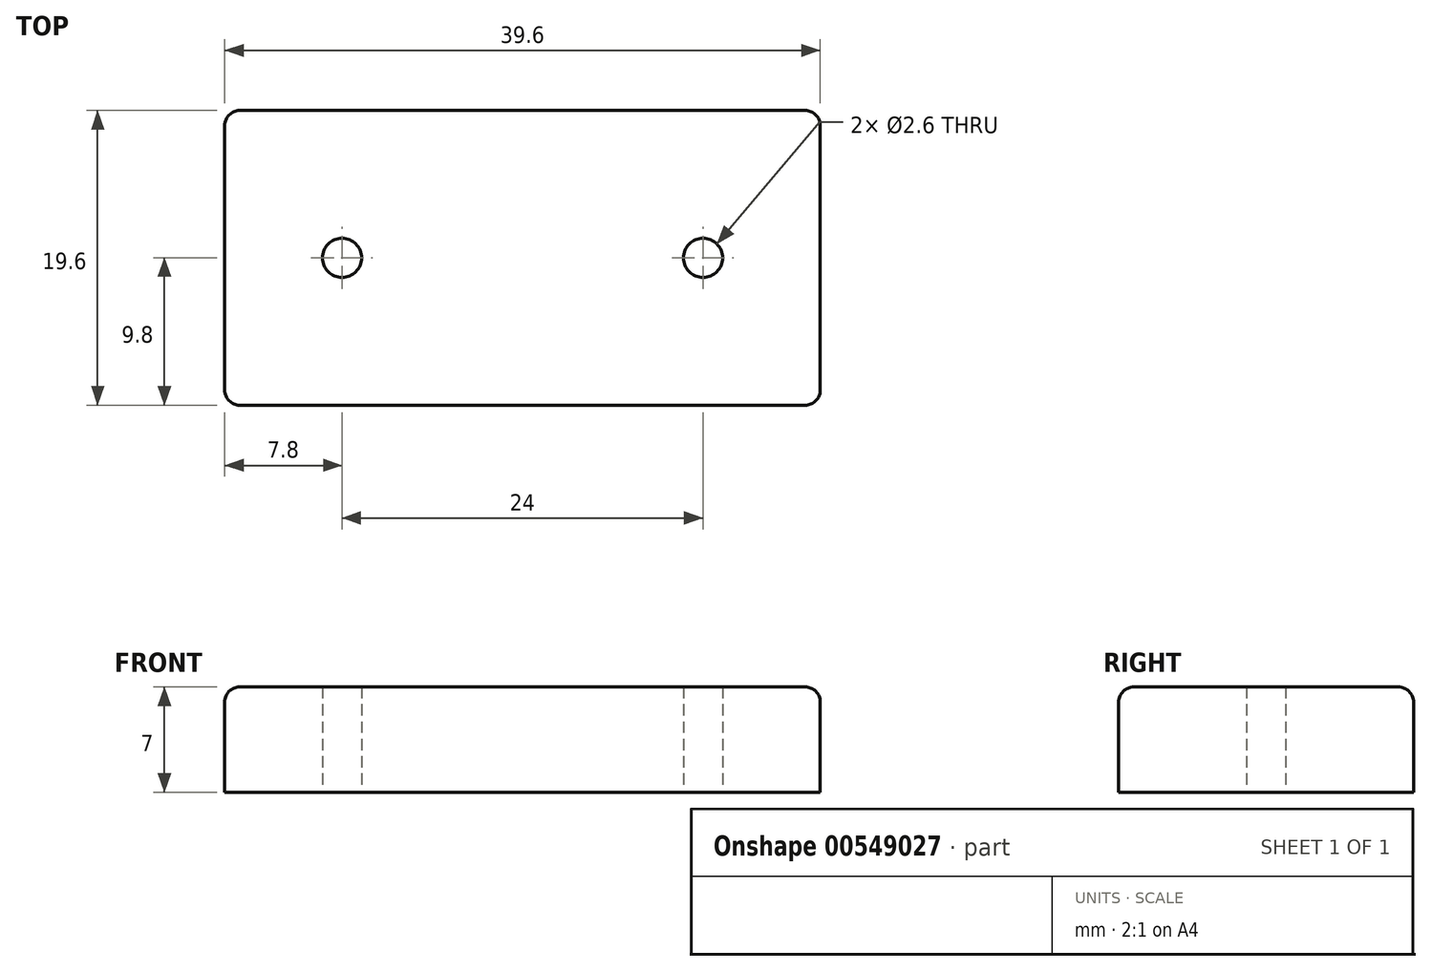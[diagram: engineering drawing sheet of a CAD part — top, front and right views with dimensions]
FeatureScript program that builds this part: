
annotation { "Feature Type Name" : "Feature", "Feature Type Description" : "" }
export const myFeature = defineFeature(function(context is Context, id is Id, definition is map)
    precondition{}
    {
        {
            var Q0;
            Q0=qCreatedBy(makeId("Top.planeOp"),FACE);
            var sketch = newSketch(context, id + "F0", { "sketchPlane" : qUnion([Q0])});
            skLineSegment(sketch, "E0.bottom", {"start": v(19.8, -9.8) * mm, "end": v(-19.8, -9.8) * mm});
            skLineSegment(sketch, "E0.top", {"start": v(19.8, 9.8) * mm, "end": v(-19.8, 9.8) * mm});
            skLineSegment(sketch, "E0.left", {"start": v(19.8, -9.8) * mm, "end": v(19.8, 9.8) * mm});
            skLineSegment(sketch, "E0.right", {"start": v(-19.8, -9.8) * mm, "end": v(-19.8, 9.8) * mm});
            skPoint(sketch, "E0.middle", {"position": v(0, 0) * mm});
            skCircle(sketch, "E1", {"center": v(12, 0) * mm, "radius": 1.3 * mm});
            skLineSegment(sketch, "E2", {"start": v(0, 0) * mm, "end": v(0, 13.8) * mm, "construction": true});
            skPoint(sketch, "E2.endSnap0", {"position": v(0, 9.8) * mm});
            skCircle(sketch, "E3.MirrorC", {"center": v(-12, 0) * mm, "radius": 1.3 * mm});
            skSolve(sketch);
        }
        {
            var Q0;
            Q0=makeQuery(id+"F0.imprint","IMPRINT",FACE,{"disambiguationData":[TD([[makeQuery(id+"F0.imprint","IMPRINT",EDGE,{"derivedFrom":sQuery(id+"F0.wireOp",EDGE,"E0.bottom")}),-1.0]])]});
            extrude(context, id + "F1", {"entities" : qUnion([Q0]), "depth" : 7 * mm, "offsetDistance" : 25 * mm});
        }
        {
            var Q0;
            Q0=makeQuery(id+"F1.opExtrude","CAP_EDGE",EDGE,{"disambiguationData":[OSD([sQuery(id+"F0.wireOp",EDGE,"E0.top")])],"isStart":false});
            var Q1;
            Q1=makeQuery(id+"F1.opExtrude","CAP_EDGE",EDGE,{"disambiguationData":[OSD([sQuery(id+"F0.wireOp",EDGE,"E0.left")])],"isStart":false});
            var Q2;
            Q2=makeQuery(id+"F1.opExtrude","CAP_EDGE",EDGE,{"disambiguationData":[OSD([sQuery(id+"F0.wireOp",EDGE,"E0.bottom")])],"isStart":false});
            var Q3;
            Q3=makeQuery(id+"F1.opExtrude","SWEPT_EDGE",EDGE,{"disambiguationData":[OSD([sQuery(id+"F0.wireOp",EDGE,"E0.top"),sQuery(id+"F0.wireOp",EDGE,"E0.left")])]});
            var Q4;
            Q4=makeQuery(id+"F1.opExtrude","SWEPT_EDGE",EDGE,{"disambiguationData":[OSD([sQuery(id+"F0.wireOp",EDGE,"E0.bottom"),sQuery(id+"F0.wireOp",EDGE,"E0.left")])]});
            var Q5;
            Q5=makeQuery(id+"F1.opExtrude","SWEPT_EDGE",EDGE,{"disambiguationData":[OSD([sQuery(id+"F0.wireOp",EDGE,"E0.bottom"),sQuery(id+"F0.wireOp",EDGE,"E0.right")])]});
            var Q6;
            Q6=makeQuery(id+"F1.opExtrude","SWEPT_EDGE",EDGE,{"disambiguationData":[OSD([sQuery(id+"F0.wireOp",EDGE,"E0.top"),sQuery(id+"F0.wireOp",EDGE,"E0.right")])]});
            var Q7;
            Q7=makeQuery(id+"F1.opExtrude","CAP_EDGE",EDGE,{"disambiguationData":[OSD([sQuery(id+"F0.wireOp",EDGE,"E0.right")])],"isStart":false});
            fillet(context, id + "F2", {"entities" : qUnion([Q0, Q1, Q2, Q3, Q4, Q5, Q6, Q7]), "radius" : 1 * mm, "tangentPropagation" : true, "allowEdgeOverflow" : false});
        }
    });
